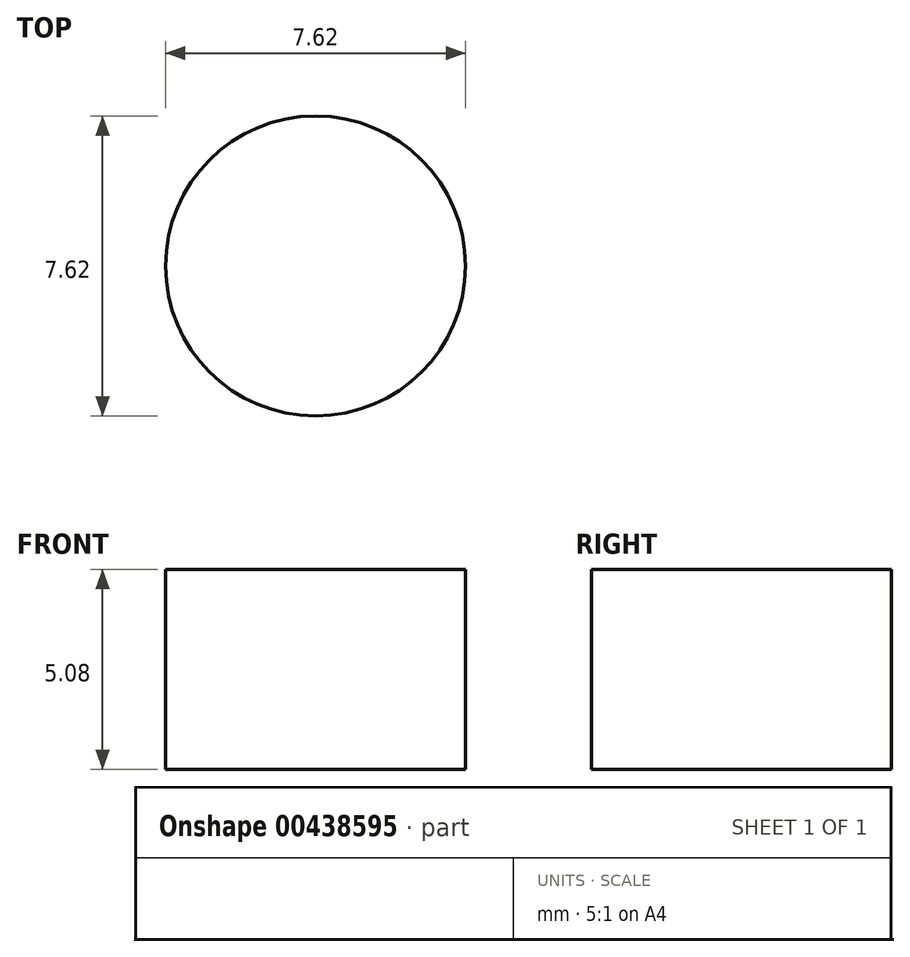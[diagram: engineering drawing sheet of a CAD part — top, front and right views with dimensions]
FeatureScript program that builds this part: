
annotation { "Feature Type Name" : "Feature", "Feature Type Description" : "" }
export const myFeature = defineFeature(function(context is Context, id is Id, definition is map)
    precondition{}
    {
        {
            var Q0;
            Q0=qCreatedBy(makeId("Top.planeOp"),FACE);
            var sketch = newSketch(context, id + "F0", { "sketchPlane" : qUnion([Q0])});
            skCircle(sketch, "E0", {"center": v(0, 0) * mm, "radius": 3.81 * mm});
            skSolve(sketch);
        }
        {
            var Q0;
            Q0=makeQuery(id+"F0.imprint","IMPRINT",FACE,{"disambiguationData":[TD([[makeQuery(id+"F0.imprint","IMPRINT",EDGE,{"derivedFrom":sQuery(id+"F0.wireOp",EDGE,"E0")}),1.0]])]});
            extrude(context, id + "F1", {"entities" : qUnion([Q0]), "depth" : 5.08 * mm});
        }
    });
